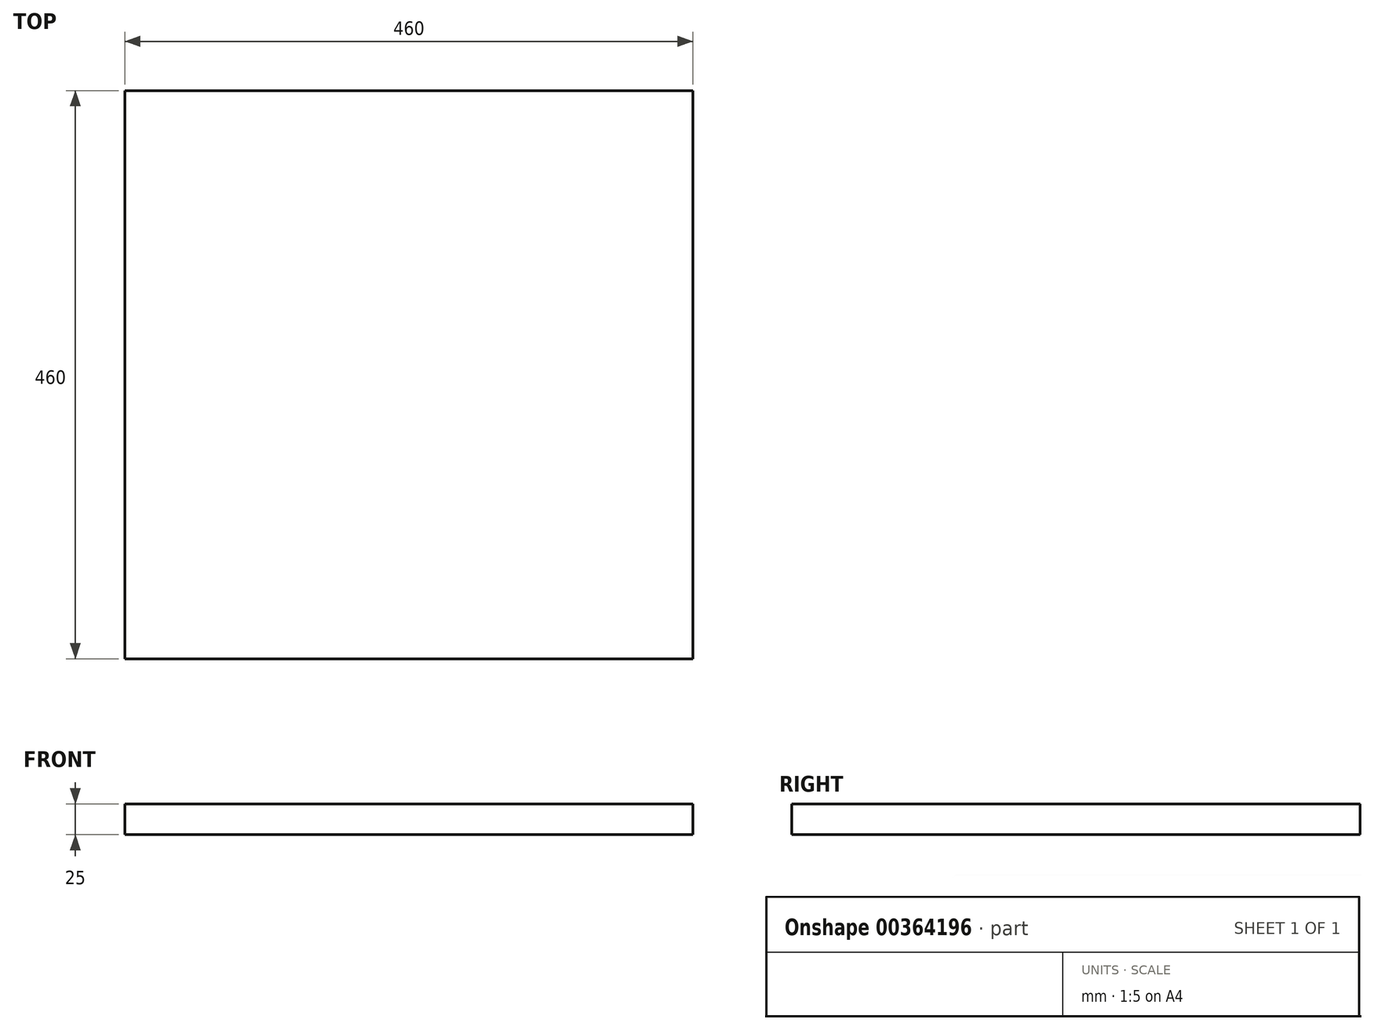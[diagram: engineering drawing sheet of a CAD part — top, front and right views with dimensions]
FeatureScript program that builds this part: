
annotation { "Feature Type Name" : "Feature", "Feature Type Description" : "" }
export const myFeature = defineFeature(function(context is Context, id is Id, definition is map)
    precondition{}
    {
        {
            var Q0;
            Q0=qCreatedBy(makeId("Top.planeOp"),FACE);
            var sketch = newSketch(context, id + "F0", { "sketchPlane" : qUnion([Q0])});
            skLineSegment(sketch, "E0.bottom", {"start": v(230, -230) * mm, "end": v(-230, -230) * mm});
            skLineSegment(sketch, "E0.top", {"start": v(230, 230) * mm, "end": v(-230, 230) * mm});
            skLineSegment(sketch, "E0.left", {"start": v(230, -230) * mm, "end": v(230, 230) * mm});
            skLineSegment(sketch, "E0.right", {"start": v(-230, -230) * mm, "end": v(-230, 230) * mm});
            skPoint(sketch, "E0.middle", {"position": v(0, 0) * mm});
            skSolve(sketch);
        }
        {
            var Q0;
            Q0=makeQuery(id+"F0.imprint","IMPRINT",FACE,{"disambiguationData":[TD([[makeQuery(id+"F0.imprint","IMPRINT",EDGE,{"derivedFrom":sQuery(id+"F0.wireOp",EDGE,"E0.bottom")}),-1.0]])]});
            extrude(context, id + "F1", {"entities" : qUnion([Q0]), "depth" : 25 * mm});
        }
    });
